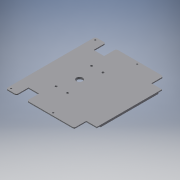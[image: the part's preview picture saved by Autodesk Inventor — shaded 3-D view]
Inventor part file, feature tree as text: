
AUTODESK INVENTOR PART (.ipt)
format: ipt  version: 2016 (Build 200138000, 138)  size: 256,512 bytes
history: native  units: in
note: dims shown in document units (in); Inventor stores cm internally (conversion verified against a paired STEP export)
features: extrude x5, sketch x5, fillet x1
ambient origin geometry x8: Origin, YZ Plane, XZ Plane, XY Plane, X Axis, Y Axis, Z Axis, Center Point
bodies: Solid1 (feature_tree)
feature tree (11):
  extrude  "Extrusion1"  Depth=0.0394in
  extrude  "Extrusion2"  Depth=0.0394in
  extrude  "Extrusion3"  Depth=0.0394in
  extrude  "Extrusion4"  Depth=0.0787in TaperAngle=0.0deg
  extrude  "Extrusion5"  Depth=0.1181in
  fillet  "Fillet1"  Radius=0.1181in
  sketch  "Sketch1"  dims[d0=0.0394in d1=0.0394in]
  sketch  "Sketch4"  dims[d2=0.0394in d3=0.0394in]
  sketch  "Sketch5"  dims[d4=0.0394in d5=0.0394in]
  sketch  "Sketch8"  dims[d6=0.0394in d8=0.0787in d9=0.0in]
  sketch  "Sketch9"  dims[d40=0.0787in d53=0.1181in d54=0.1181in d55=0.1181in d56=0.1181in d57=0.1181in d58=0.1181in d59=0.2756in d60=0.1181in d61=0.1181in d62=0.1181in d63=0.2756in d65=0.0787in d66=0.0in d67=0.1575in d68=0.0in d71=0.4724in d72=0.5512in d73=0.1772in d74=0.1575in d75=1.3386in d76=0.1575in d77=2.7921in d78=0.7874in d79=0.1575in d80=3.3465in d82=0.1969in d83=0.0in d84=0.2362in d85=0.2362in d86=0.1181in d87=0.1181in d88=0.1181in d89=0.2362in d90=0.1181in d91=0.2362in d92=0.4331in d93=0.0in d94=0.1181in d97=0.0394in d99=3.3071in d100=0.9843in d101=1.063in d102=0.0394in d103=5.7874in d104=0.0394in]
